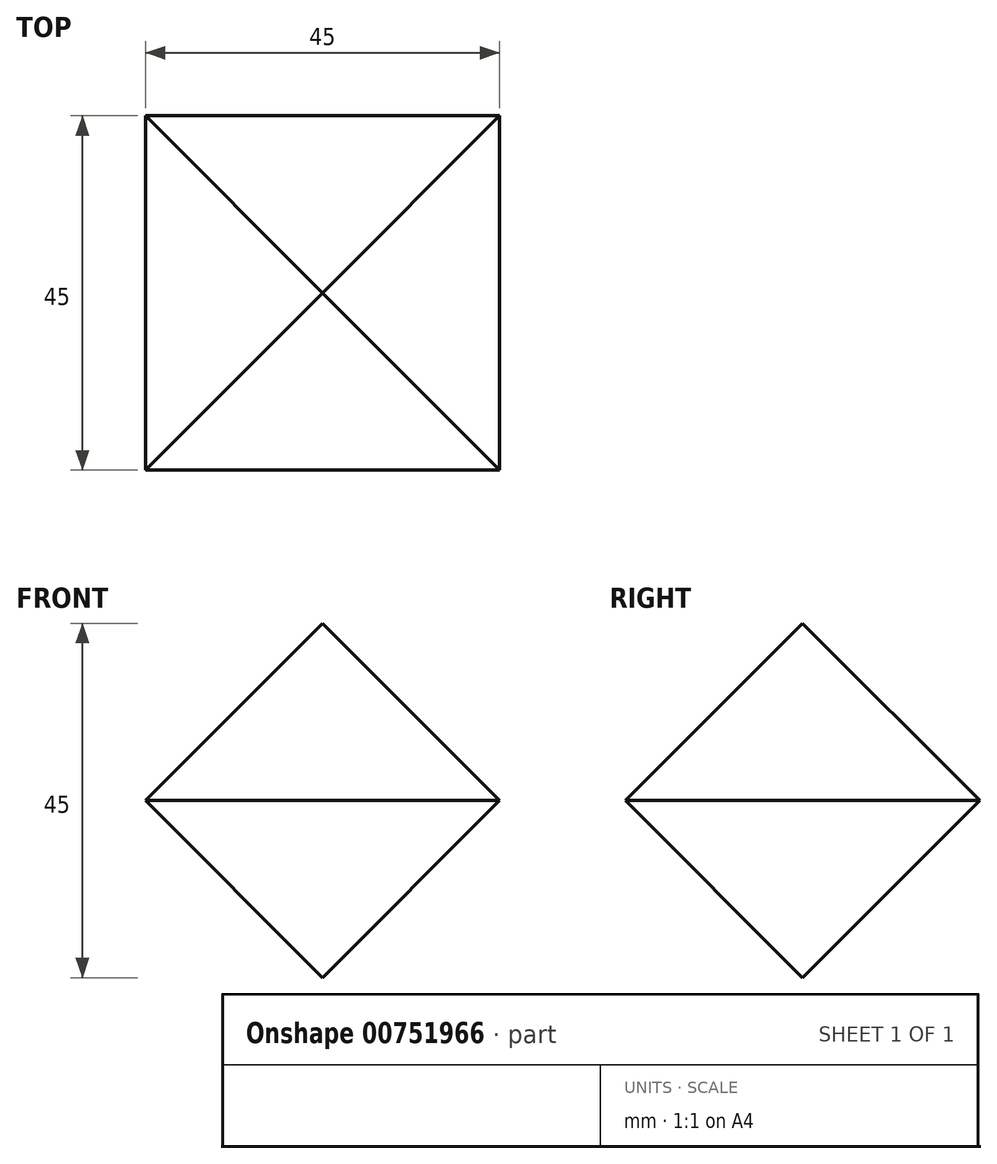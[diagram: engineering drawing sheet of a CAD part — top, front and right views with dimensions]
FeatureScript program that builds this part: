
annotation { "Feature Type Name" : "Feature", "Feature Type Description" : "" }
export const myFeature = defineFeature(function(context is Context, id is Id, definition is map)
    precondition{}
    {
        {
            var Q0;
            Q0=qCreatedBy(makeId("Top.planeOp"),FACE);
            var sketch = newSketch(context, id + "F0", { "sketchPlane" : qUnion([Q0])});
            skLineSegment(sketch, "E0.bottom", {"start": v(-22.5, 22.5) * mm, "end": v(22.5, 22.5) * mm});
            skLineSegment(sketch, "E0.top", {"start": v(-22.5, -22.5) * mm, "end": v(22.5, -22.5) * mm});
            skLineSegment(sketch, "E0.left", {"start": v(-22.5, 22.5) * mm, "end": v(-22.5, -22.5) * mm});
            skLineSegment(sketch, "E0.right", {"start": v(22.5, 22.5) * mm, "end": v(22.5, -22.5) * mm});
            skPoint(sketch, "E0.middle", {"position": v(0, 0) * mm});
            skSolve(sketch);
        }
        {
            var Q0;
            Q0=makeQuery(id+"F0.imprint","IMPRINT",FACE,{"disambiguationData":[TD([[makeQuery(id+"F0.imprint","IMPRINT",EDGE,{"derivedFrom":sQuery(id+"F0.wireOp",EDGE,"E0.bottom")}),-1.0]])]});
            extrude(context, id + "F1", {"entities" : qUnion([Q0]), "endBound" : BoundingType.SYMMETRIC, "depth" : 50.8 * mm, "offsetDistance" : 25.4 * mm, "hasDraft" : true, "draftAngle" : 45 * degree, "draftPullDirection" : true});
        }
    });
